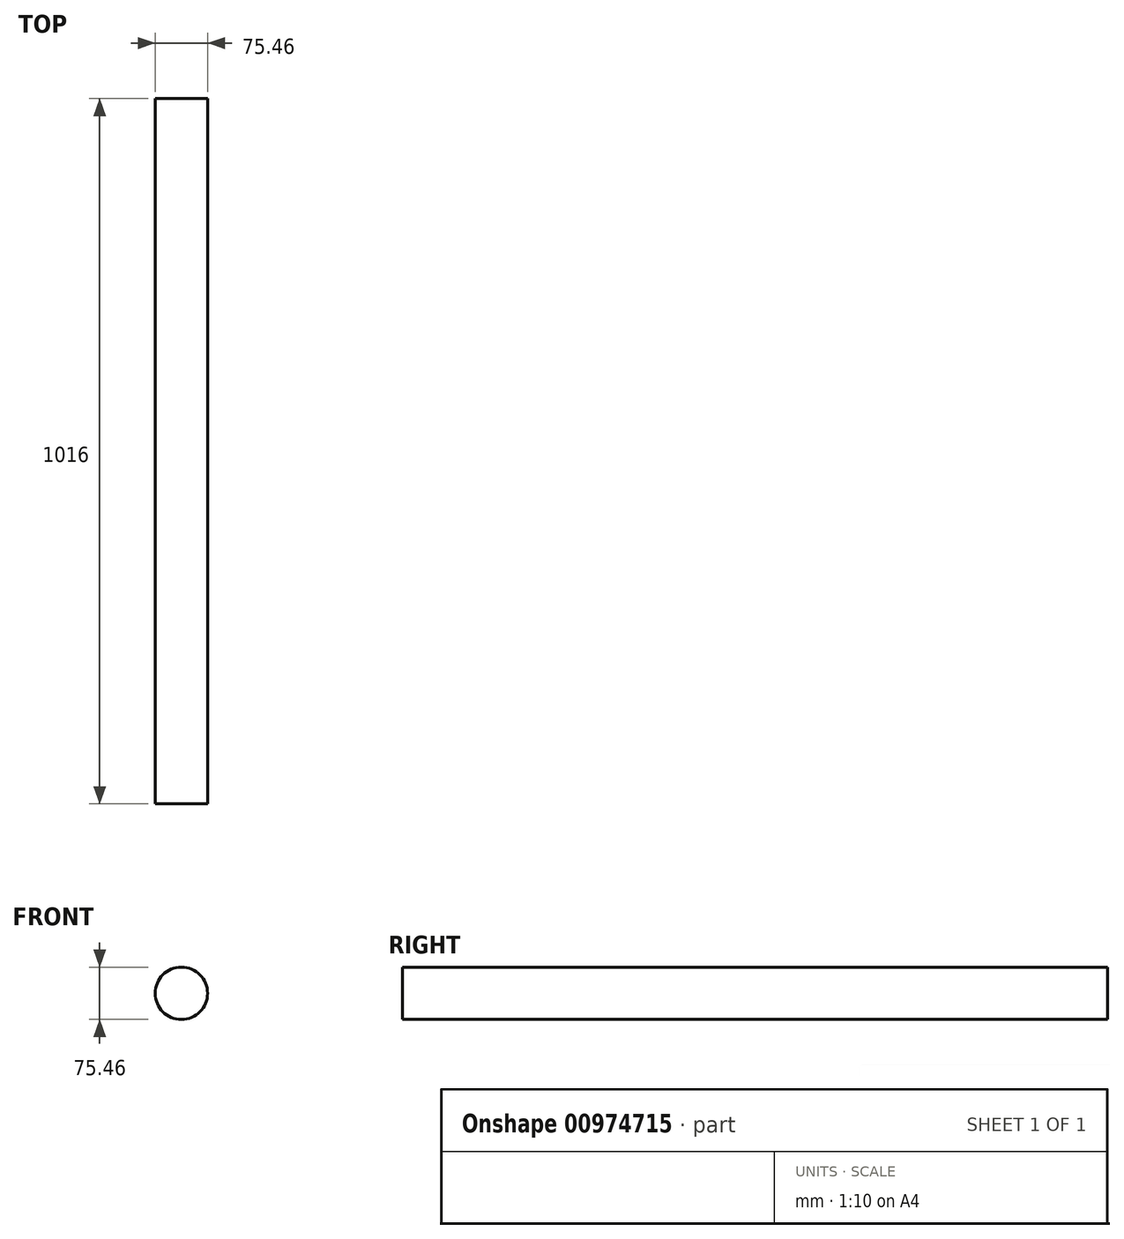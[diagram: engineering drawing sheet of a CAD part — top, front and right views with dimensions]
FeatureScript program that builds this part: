
annotation { "Feature Type Name" : "Feature", "Feature Type Description" : "" }
export const myFeature = defineFeature(function(context is Context, id is Id, definition is map)
    precondition{}
    {
        {
            var Q0;
            Q0=qCreatedBy(makeId("Front.planeOp"),FACE);
            var sketch = newSketch(context, id + "F0", { "sketchPlane" : qUnion([Q0])});
            skCircle(sketch, "E0", {"center": v(0, 0) * mm, "radius": 55.73 * mm, "construction": true});
            skCircle(sketch, "E1", {"center": v(0, 0) * mm, "radius": 37.73 * mm});
            skSolve(sketch);
        }
        {
            var Q0;
            Q0=makeQuery(id+"F0.imprint","IMPRINT",FACE,{"disambiguationData":[TD([[makeQuery(id+"F0.imprint","IMPRINT",EDGE,{"derivedFrom":sQuery(id+"F0.wireOp",EDGE,"E1")}),1.0]])]});
            var Q1;
            Q1 = qBodyType(qCreatedBy(id + "F0" ,EDGE), BodyType.WIRE);
            var Q2;
            Q2=sQuery(id+"F0.wireOp",EDGE,"E1");
            extrude(context, id + "F1", {"entities" : qUnion([Q0]), "surfaceEntities" : qUnion([Q1, Q2]), "endBound" : BoundingType.SYMMETRIC, "depth" : 1016 * mm, "offsetDistance" : 25.4 * mm});
        }
    });
